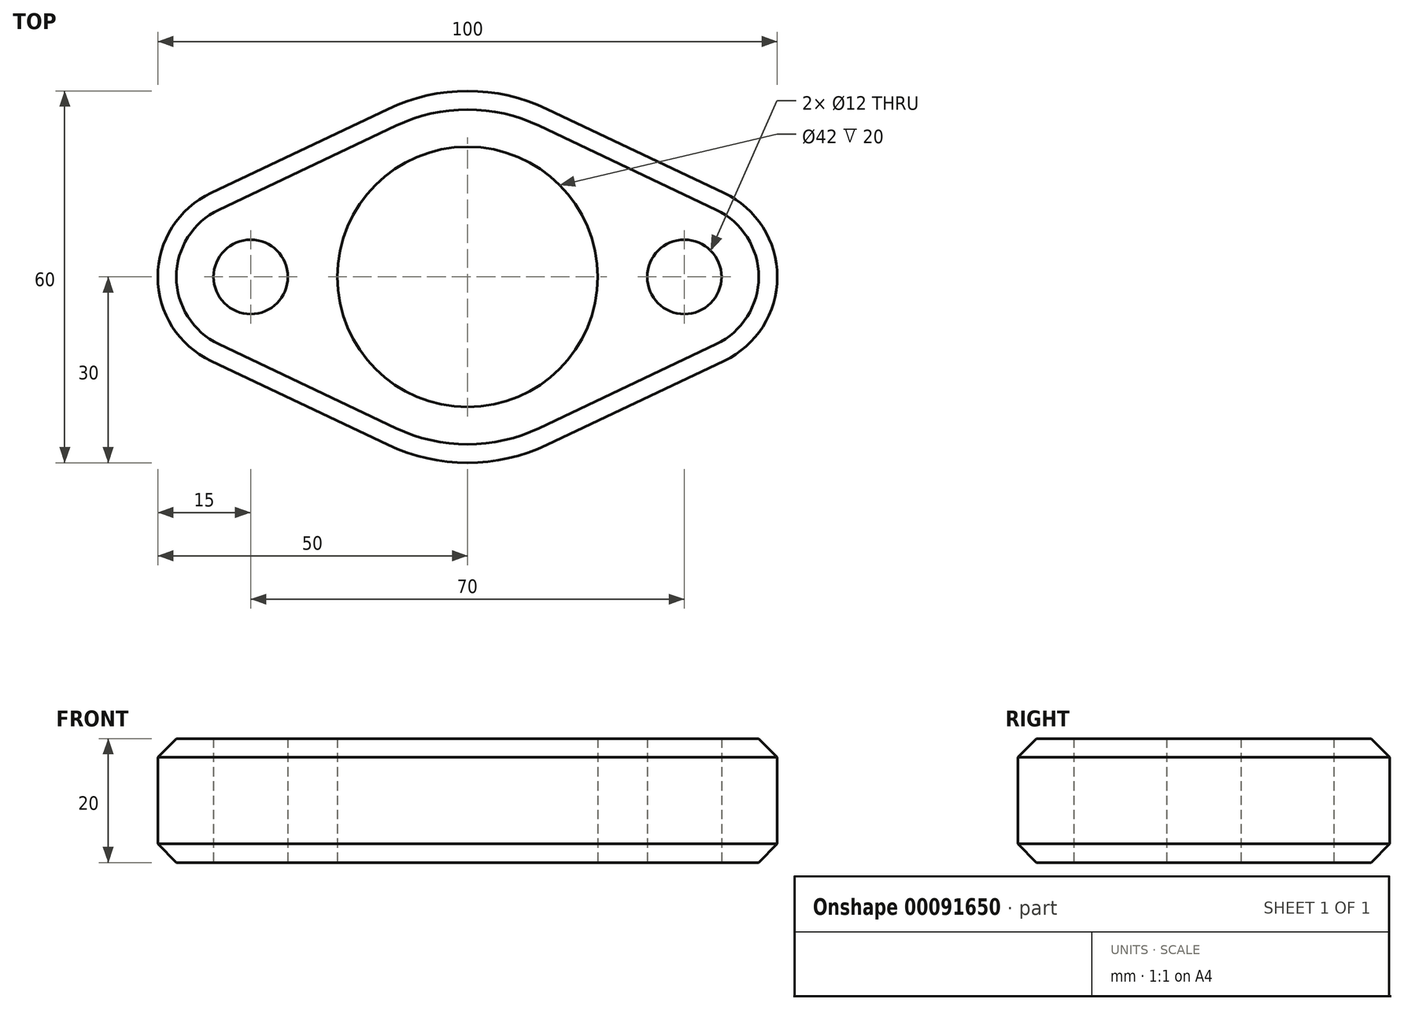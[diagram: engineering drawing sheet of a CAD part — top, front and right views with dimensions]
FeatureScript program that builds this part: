
annotation { "Feature Type Name" : "Feature", "Feature Type Description" : "" }
export const myFeature = defineFeature(function(context is Context, id is Id, definition is map)
    precondition{}
    {
        {
            var Q0;
            Q0=qCreatedBy(makeId("Top.planeOp"),FACE);
            var sketch = newSketch(context, id + "F0", { "sketchPlane" : qUnion([Q0])});
            skArc(sketch, "E0", {"start": v(12.86, 27.1) * mm, "mid": v(0, 30) * mm, "end": v(-12.86, 27.1) * mm});
            skArc(sketch, "E1", {"start": v(41.43, -13.55) * mm, "mid": v(50, 0) * mm, "end": v(41.43, 13.55) * mm});
            skLineSegment(sketch, "E2", {"start": v(12.86, 27.1) * mm, "end": v(41.43, 13.55) * mm});
            skLineSegment(sketch, "E3", {"start": v(12.86, -27.1) * mm, "end": v(41.43, -13.55) * mm});
            skLineSegment(sketch, "E4.MirrorCS", {"start": v(-12.86, 27.1) * mm, "end": v(-41.43, 13.55) * mm});
            skArc(sketch, "E5.MirrorCS", {"start": v(-41.43, -13.55) * mm, "mid": v(-50, 0) * mm, "end": v(-41.43, 13.55) * mm});
            skLineSegment(sketch, "E6.MirrorCS", {"start": v(-12.86, -27.1) * mm, "end": v(-41.43, -13.55) * mm});
            skArc(sketch, "E7.trimOffspring", {"start": v(-12.86, -27.1) * mm, "mid": v(0, -30) * mm, "end": v(12.86, -27.1) * mm});
            skCircle(sketch, "E8", {"center": v(35, 0) * mm, "radius": 6 * mm});
            skCircle(sketch, "E9.MirrorC", {"center": v(-35, 0) * mm, "radius": 6 * mm});
            skCircle(sketch, "E10", {"center": v(0, 0) * mm, "radius": 21 * mm});
            skLineSegment(sketch, "E11", {"start": v(-62.77, 0) * mm, "end": v(62.56, 0) * mm, "construction": true});
            skSolve(sketch);
        }
        {
            var Q0;
            Q0=makeQuery(id+"F0.imprint","IMPRINT",FACE,{"disambiguationData":[TD([[makeQuery(id+"F0.imprint","IMPRINT",EDGE,{"derivedFrom":sQuery(id+"F0.wireOp",EDGE,"E0")}),1.0]])]});
            extrude(context, id + "F1", {"entities" : qUnion([Q0]), "depth" : 10 * mm});
        }
        {
            var Q0;
            Q0=makeQuery(id+"F1.opExtrude","CAP_EDGE",EDGE,{"disambiguationData":[OSD([sQuery(id+"F0.wireOp",EDGE,"E6.MirrorCS")])],"isStart":false});
            var Q1;
            Q1=makeQuery(id+"F1.opExtrude","CAP_EDGE",EDGE,{"disambiguationData":[OSD([sQuery(id+"F0.wireOp",EDGE,"E7.trimOffspring")])],"isStart":false});
            var Q2;
            Q2=makeQuery(id+"F1.opExtrude","CAP_EDGE",EDGE,{"disambiguationData":[OSD([sQuery(id+"F0.wireOp",EDGE,"E3")])],"isStart":false});
            chamfer(context, id + "F2", {"entities" : qUnion([Q0, Q1, Q2]), "width" : 3 * mm, "tangentPropagation" : true});
        }
        {
            var Q0;
            Q0=makeQuery(id+"F1.opExtrude","SWEPT_BODY",BODY,{"disambiguationData":[OSD([sQuery(id+"F0.wireOp",EDGE,"E0"),sQuery(id+"F0.wireOp",EDGE,"E1"),sQuery(id+"F0.wireOp",EDGE,"E2"),sQuery(id+"F0.wireOp",EDGE,"E3"),sQuery(id+"F0.wireOp",EDGE,"E4.MirrorCS"),sQuery(id+"F0.wireOp",EDGE,"E5.MirrorCS"),sQuery(id+"F0.wireOp",EDGE,"E6.MirrorCS"),sQuery(id+"F0.wireOp",EDGE,"E7.trimOffspring"),sQuery(id+"F0.wireOp",EDGE,"E8"),sQuery(id+"F0.wireOp",EDGE,"E9.MirrorC"),sQuery(id+"F0.wireOp",EDGE,"E10")])]});
            var Q1;
            Q1=makeQuery(id+"F0.imprint","IMPRINT",FACE,{"disambiguationData":[TD([[makeQuery(id+"F0.imprint","IMPRINT",EDGE,{"derivedFrom":sQuery(id+"F0.wireOp",EDGE,"E0")}),1.0]])]});
            mirror(context, id + "F3", {"operationType" : NewBodyOperationType.ADD, "entities" : qUnion([Q0]), "mirrorPlane" : qUnion([Q1])});
        }
    });
